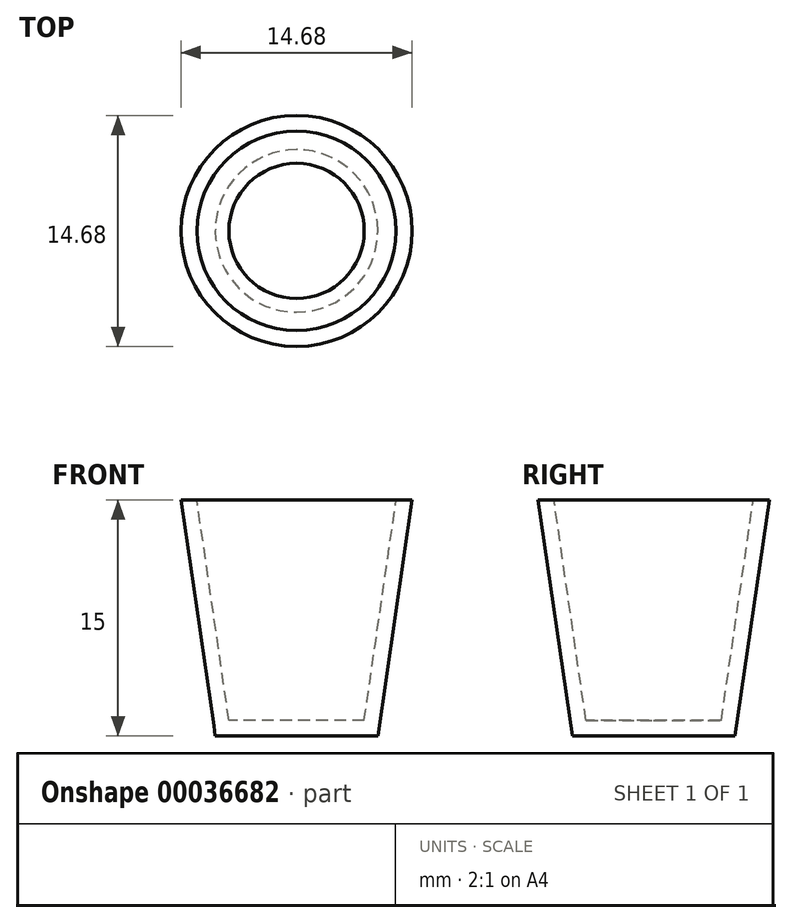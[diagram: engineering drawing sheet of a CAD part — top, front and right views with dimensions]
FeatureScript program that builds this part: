
annotation { "Feature Type Name" : "Feature", "Feature Type Description" : "" }
export const myFeature = defineFeature(function(context is Context, id is Id, definition is map)
    precondition{}
    {
        {
            var Q0;
            Q0=qCreatedBy(makeId("Front.planeOp"),FACE);
            var sketch = newSketch(context, id + "F0", { "sketchPlane" : qUnion([Q0])});
            skLineSegment(sketch, "E0", {"start": v(-7.34, 10.12) * mm, "end": v(-5.16, -4.88) * mm});
            skLineSegment(sketch, "E1", {"start": v(-5.16, -4.88) * mm, "end": v(0, -4.88) * mm});
            skLineSegment(sketch, "E2", {"start": v(0, -4.88) * mm, "end": v(0, 10.12) * mm});
            skLineSegment(sketch, "E3", {"start": v(0, 10.12) * mm, "end": v(-7.34, 10.12) * mm});
            skSolve(sketch);
        }
        {
            var Q0;
            Q0=makeQuery(id+"F0.imprint","IMPRINT",FACE,{"disambiguationData":[TD([[makeQuery(id+"F0.imprint","IMPRINT",EDGE,{"derivedFrom":sQuery(id+"F0.wireOp",EDGE,"E0")}),1.0]])]});
            var Q1;
            Q1=sQuery(id+"F0.wireOp",EDGE,"E2");
            revolve(context, id + "F1", {"entities" : qUnion([Q0]), "axis" : qUnion([Q1]), "revolveType" : RevolveType.FULL});
        }
        {
            var Q0;
            Q0=makeQuery(id+"F1.opRevolve","SWEPT_FACE",FACE,{"disambiguationData":[OSD([sQuery(id+"F0.wireOp",EDGE,"E3")])]});
            shell(context, id + "F2", {"entities" : qUnion([Q0]), "thickness" : 1 * mm});
        }
    });
